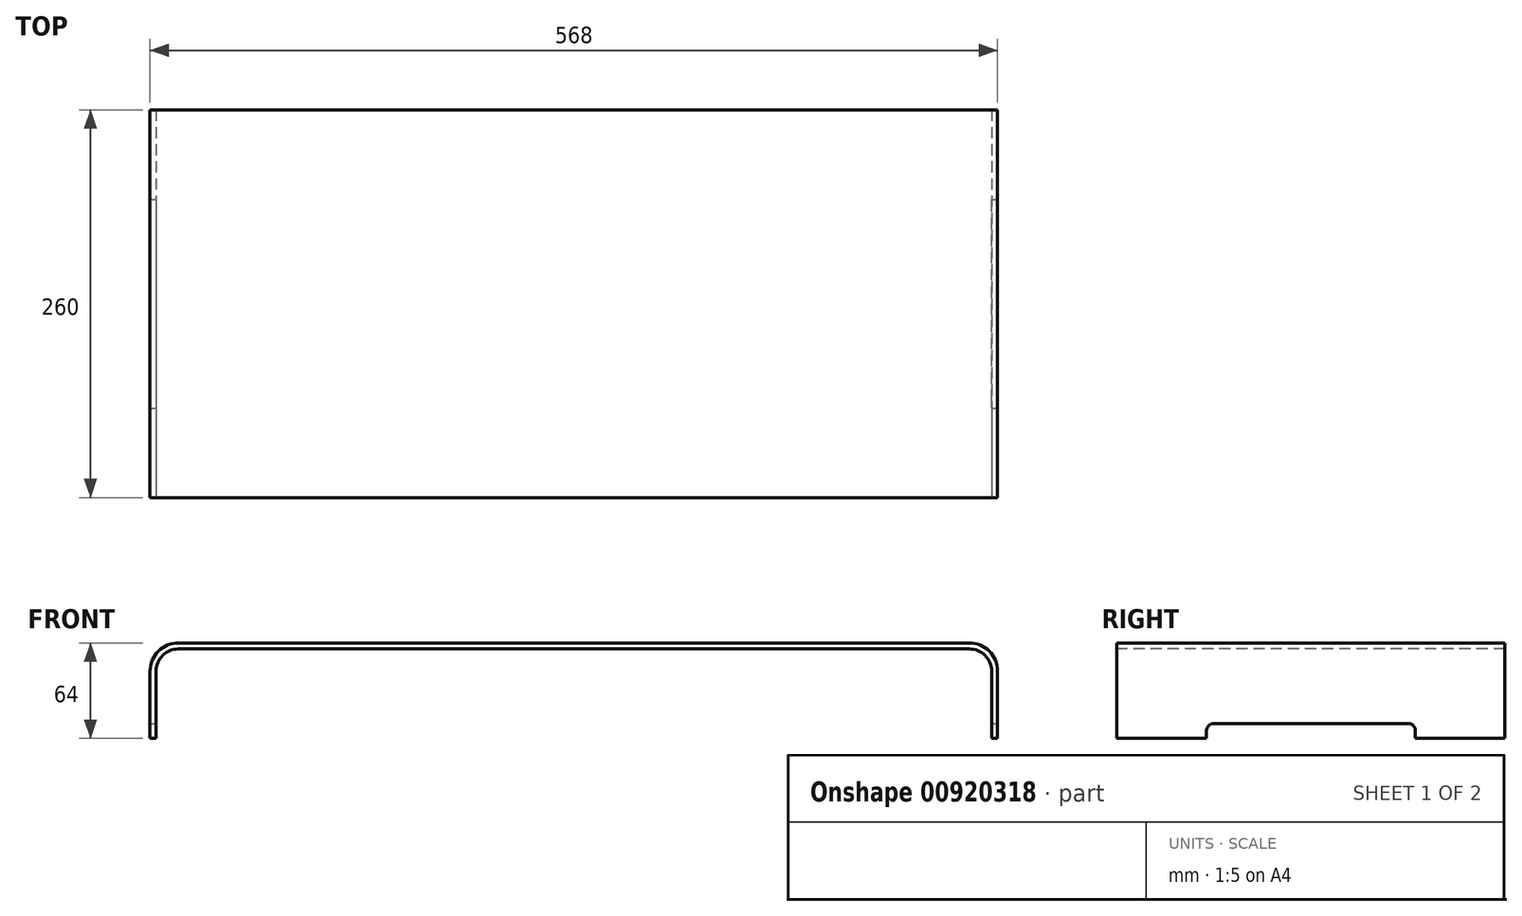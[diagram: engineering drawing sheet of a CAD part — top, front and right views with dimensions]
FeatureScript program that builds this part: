
annotation { "Feature Type Name" : "Feature", "Feature Type Description" : "" }
export const myFeature = defineFeature(function(context is Context, id is Id, definition is map)
    precondition{}
    {
        {
            var Q0;
            Q0=qCreatedBy(makeId("Front.planeOp"),FACE);
            var sketch = newSketch(context, id + "F0", { "sketchPlane" : qUnion([Q0])});
            skLineSegment(sketch, "E0", {"start": v(-246.13, -45) * mm, "end": v(-246.13, 0) * mm});
            skLineSegment(sketch, "E1", {"start": v(-231.13, 15) * mm, "end": v(298.87, 15) * mm});
            skLineSegment(sketch, "E2", {"start": v(313.87, 0) * mm, "end": v(313.87, -45) * mm});
            skArc(sketch, "E3", {"start": v(-231.13, 15) * mm, "mid": v(-241.73, 10.6) * mm, "end": v(-246.13, 0) * mm});
            skArc(sketch, "E4", {"start": v(313.87, 0) * mm, "mid": v(309.48, 10.6) * mm, "end": v(298.87, 15) * mm});
            skLineSegment(sketch, "E5.0", {"start": v(317.87, 0) * mm, "end": v(317.87, -45) * mm});
            skLineSegment(sketch, "E5.1", {"start": v(-250.13, -45) * mm, "end": v(-250.13, 0) * mm});
            skArc(sketch, "E5.2", {"start": v(-231.13, 19) * mm, "mid": v(-244.56, 13.44) * mm, "end": v(-250.13, 0) * mm});
            skLineSegment(sketch, "E5.3", {"start": v(-231.13, 19) * mm, "end": v(298.87, 19) * mm});
            skArc(sketch, "E5.4", {"start": v(317.87, 0) * mm, "mid": v(312.3, 13.44) * mm, "end": v(298.87, 19) * mm});
            skLineSegment(sketch, "E6", {"start": v(-246.13, -45) * mm, "end": v(-250.13, -45) * mm});
            skLineSegment(sketch, "E7", {"start": v(313.87, -45) * mm, "end": v(317.87, -45) * mm});
            skSolve(sketch);
        }
        {
            var Q0;
            Q0=makeQuery(id+"F0.imprint","IMPRINT",FACE,{"disambiguationData":[TD([[makeQuery(id+"F0.imprint","IMPRINT",EDGE,{"derivedFrom":sQuery(id+"F0.wireOp",EDGE,"E0")}),1.0]])]});
            extrude(context, id + "F1", {"entities" : qUnion([Q0]), "oppositeDirection" : true, "depth" : 260 * mm, "offsetDistance" : 25 * mm, "symmetric" : true});
        }
        {
            var Q0;
            Q0=makeQuery(id+"F1.opExtrude","SWEPT_FACE",FACE,{"disambiguationData":[OSD([sQuery(id+"F0.wireOp",EDGE,"E5.0")])]});
            var sketch = newSketch(context, id + "F2", { "sketchPlane" : qUnion([Q0])});
            skLineSegment(sketch, "E8.bottom", {"start": v(70, -45) * mm, "end": v(-70, -45) * mm});
            skLineSegment(sketch, "E8.top", {"start": v(70, -35) * mm, "end": v(-70, -35) * mm});
            skLineSegment(sketch, "E8.left", {"start": v(70, -45) * mm, "end": v(70, -35) * mm});
            skLineSegment(sketch, "E8.right", {"start": v(-70, -45) * mm, "end": v(-70, -35) * mm});
            skArc(sketch, "E9", {"start": v(-65, -35) * mm, "mid": v(-68.54, -36.46) * mm, "end": v(-70, -40) * mm});
            skArc(sketch, "E10", {"start": v(70, -40) * mm, "mid": v(68.54, -36.46) * mm, "end": v(65, -35) * mm});
            skSolve(sketch);
        }
        {
            var Q0;
            {var subQ1=sQuery(id+"F2.wireOp",EDGE,"E8.bottom");Q0=makeQuery(id+"F2.imprint","IMPRINT",FACE,{"disambiguationData":[TD([[makeQuery(id+"F2.imprint","IMPRINT",EDGE,{"derivedFrom":subQ1}),-1.0]])]});}
            extrude(context, id + "F3", {"entities" : qUnion([Q0]), "operationType" : NewBodyOperationType.REMOVE, "oppositeDirection" : true, "depth" : 600 * mm, "offsetDistance" : 25 * mm});
        }
    });
